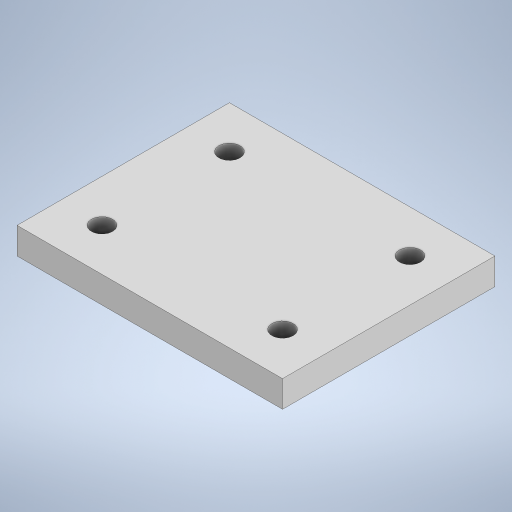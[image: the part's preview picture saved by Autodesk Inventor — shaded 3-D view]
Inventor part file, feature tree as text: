
AUTODESK INVENTOR PART (.ipt)
format: ipt  version: 2024.2 (Build 282272000, 272)  size: 218,112 bytes
history: native  units: in
note: dims shown in document units (in); Inventor stores cm internally (conversion verified against a paired STEP export)
features: extrude x1, sketch x1
ambient origin geometry x8: Origin, YZ Plane, XZ Plane, XY Plane, X Axis, Y Axis, Z Axis, Center Point
bodies: Solid1 (feature_tree)
feature tree (2):
  extrude  "Extrusion1"  Depth=1.0in
  sketch  "Sketch1"  dims[d0=1.25in d1=1.0in d2=0.1in d3=0.1in d4=0.1in d5=0.1in d6=0.6in d7=0.85in d8=0.0in d9=0.0in d10=0.0in d11=0.0in d12=0.2in d13=0.2in d14=0.125in d15=0.0in]
